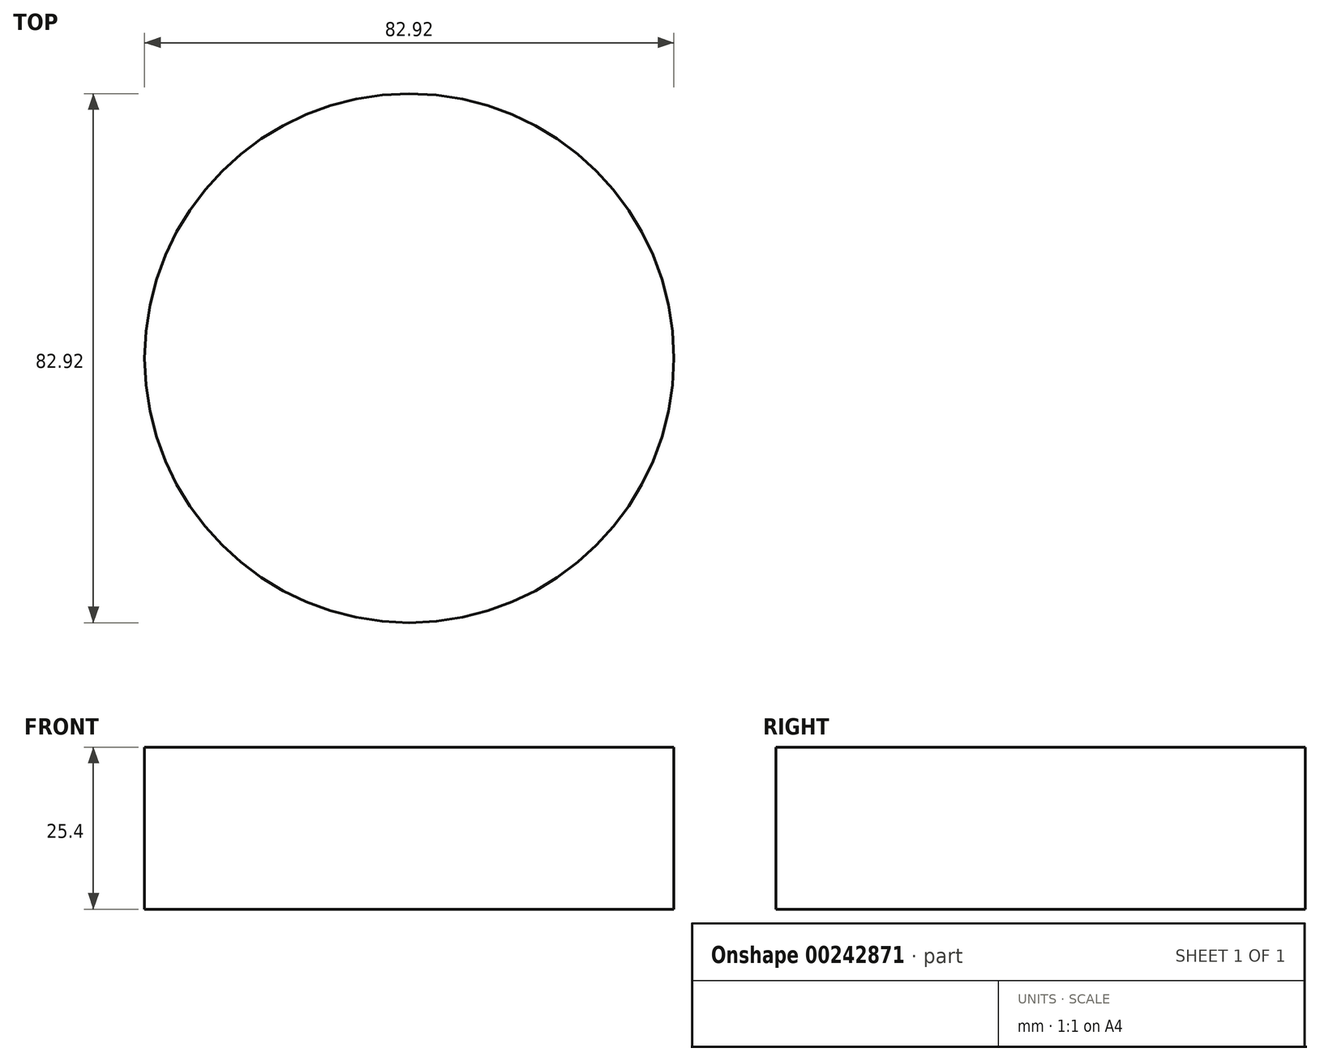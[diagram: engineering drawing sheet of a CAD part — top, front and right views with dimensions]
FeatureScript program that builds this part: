
annotation { "Feature Type Name" : "Feature", "Feature Type Description" : "" }
export const myFeature = defineFeature(function(context is Context, id is Id, definition is map)
    precondition{}
    {
        {
            var Q0;
            Q0=qCreatedBy(makeId("Top.planeOp"),FACE);
            var sketch = newSketch(context, id + "F0", { "sketchPlane" : qUnion([Q0])});
            skCircle(sketch, "E0", {"center": v(0, 0) * mm, "radius": 41.46 * mm});
            skSolve(sketch);
        }
        {
            var Q0;
            Q0=makeQuery(id+"F0.imprint","IMPRINT",FACE,{"disambiguationData":[TD([[makeQuery(id+"F0.imprint","IMPRINT",EDGE,{"derivedFrom":sQuery(id+"F0.wireOp",EDGE,"E0")}),1.0]])]});
            extrude(context, id + "F1", {"entities" : qUnion([Q0]), "depth" : 25.4 * mm});
        }
    });
